# Revit family: EN_MEADRAIN_DM_CITY_Basic
name_source: partatom
category: Allgemeines Modell
revit_build: Autodesk Revit 2018 (Build: 20170223_1515(x64)
units: mm (PartAtom-declared; Revit-internal decimal feet)

## family parameters
Beim Laden mit Abzugskörper schneiden = Ja
Bemaßung runder Anschluss = Durchmesser verwenden
Gemeinsam genutzt = Nein
Kann Basisbauteil für Bewehrung sein = Nein
Raumberechnungspunkt = Nein
Teiletyp = Normal

## types (3) — shared parameters
B_diameter inside_Outlet = 180 mm  [stored 0.590551 ft]
Bauelement = Drainage channels surface water
Beschreibung = Universal drainage system made of Polymerbeton for loading class up to D400
Building material, bedding/foundation = gemäß Zeichnung und Einzelbeschreibung
Cover = Ductile iron
Def Loading class_channel = D400
Endcap_Thickness = 3 mm  [stored 0.00984252 ft]
Hersteller = MEA Bautechnik GmbH business unit MEA Water Management
Hersteller und Typ- Ausschreibender gleichwertig = like MEA Bautechnik GmbH, Modell MEADRAIN DM
IfcDescription = Universal drainage system made of Polymerbeton for loading class up to D400
IfcExportAs = IfcWasteTerminalType
IfcExportType = USERDEFINED
Installation technology = Typ M
Length_Outlet_Inspection element = 180 mm  [stored 0.590551 ft]
Length_Outlet_gully = 194 mm
MEA_planning assistance = einschl. Fundament und Ummantelung
Modell = MEADRAIN DM
Product website = https://www.mea-group.com
Slope type / percen drainage = Ohne Gefälle
Suitability drainage component = For use in urban areas
Typ Entwässerungsbauteil = Beton
Typenkommentare = For use in urban areas
component drainage = Entwässerungsrinne
construction drainage = D400
diameter outside_Outlet_Inspection element = 200 mm  [stored 0.656168 ft]
fondation_width = 200 mm  [stored 0.656168 ft]
guid = cf6c1bd8-9bf4-4563-8c57-07955e2378ac
technical Product information = https://www.mea-group.com
zero-valued in all types: type Material channel

## per-type parameters (varying)
| type | B_H01 | B_Width | Clear width | Height | MEA- Clear width | Width_channel | arcticle number_channel | hilfstype |
| DM CITY 1000 | 225 mm  [stored 0.738189 ft] | 133 mm  [stored 0.436352 ft] | 100 mm  [stored 0.328084 ft] | 225 mm  [stored 0.738189 ft] | 1000 | 133 mm  [stored 0.436352 ft] | 010712887 | 1 |
| DM CITY 1500 | 270 mm  [stored 0.885827 ft] | 183 mm | 150 mm  [stored 0.492126 ft] | 270 mm  [stored 0.885827 ft] | 1500 | 183 mm | 010712379 | 2 |
| DM CITY 2000 | 330 mm | 233 mm  [stored 0.764436 ft] | 200 mm  [stored 0.656168 ft] | 330 mm | 2000 | 233 mm  [stored 0.764436 ft] | 010712373 | 3 |

note: [stored X ft] marks values corroborated as IEEE doubles in the binary element streams (Revit-internal decimal feet)
